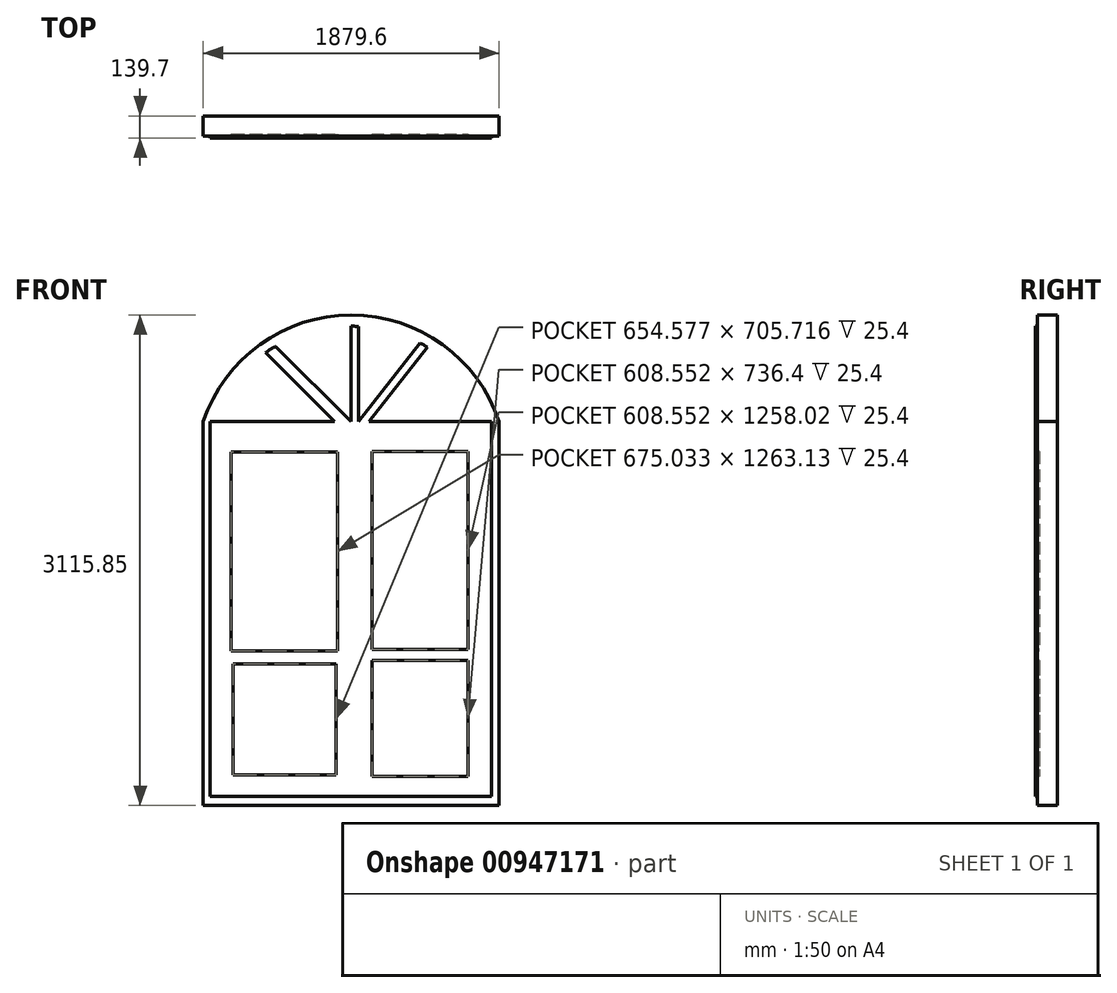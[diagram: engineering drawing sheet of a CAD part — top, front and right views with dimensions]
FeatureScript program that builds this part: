
annotation { "Feature Type Name" : "Feature", "Feature Type Description" : "" }
export const myFeature = defineFeature(function(context is Context, id is Id, definition is map)
    precondition{}
    {
        {
            var Q0;
            Q0=qCreatedBy(makeId("Front.planeOp"),FACE);
            var sketch = newSketch(context, id + "F0", { "sketchPlane" : qUnion([Q0])});
            skLineSegment(sketch, "E0.bottom", {"start": v(0, 0) * mm, "end": v(1879.6, 0) * mm});
            skLineSegment(sketch, "E0.top", {"start": v(0, 2438.4) * mm, "end": v(1879.6, 2438.4) * mm});
            skLineSegment(sketch, "E0.left", {"start": v(0, 0) * mm, "end": v(0, 2438.4) * mm});
            skLineSegment(sketch, "E0.right", {"start": v(1879.6, 0) * mm, "end": v(1879.6, 2438.4) * mm});
            skArc(sketch, "E1", {"start": v(1879.6, 2438.4) * mm, "mid": v(939.8, 3115.85) * mm, "end": v(0, 2438.4) * mm});
            skLineSegment(sketch, "E2.bottom", {"start": v(25.4, 2413) * mm, "end": v(1854.2, 2413) * mm});
            skLineSegment(sketch, "E2.top", {"start": v(25.4, 25.4) * mm, "end": v(1854.2, 25.4) * mm});
            skLineSegment(sketch, "E2.left", {"start": v(25.4, 2413) * mm, "end": v(25.4, 25.4) * mm});
            skLineSegment(sketch, "E2.right", {"start": v(1854.2, 2413) * mm, "end": v(1854.2, 25.4) * mm});
            skSolve(sketch);
        }
        {
            var Q0;
            Q0=makeQuery(id+"F0.imprint","IMPRINT",FACE,{"disambiguationData":[TD([[makeQuery(id+"F0.imprint","IMPRINT",EDGE,{"derivedFrom":sQuery(id+"F0.wireOp",EDGE,"E2.bottom")}),-1.0]])]});
            var Q1;
            Q1=makeQuery(id+"F0.imprint","IMPRINT",FACE,{"disambiguationData":[TD([[makeQuery(id+"F0.imprint","IMPRINT",EDGE,{"derivedFrom":sQuery(id+"F0.wireOp",EDGE,"E0.top")}),1.0]])]});
            var Q2;
            Q2=makeQuery(id+"F0.imprint","IMPRINT",FACE,{"disambiguationData":[TD([[makeQuery(id+"F0.imprint","IMPRINT",EDGE,{"derivedFrom":sQuery(id+"F0.wireOp",EDGE,"E0.bottom")}),1.0]])]});
            extrude(context, id + "F1", {"entities" : qUnion([Q0, Q1, Q2]), "depth" : 127 * mm, "offsetDistance" : 25.4 * mm});
        }
        {
            var Q0;
            Q0=makeQuery(id+"F1.opExtrude","CAP_FACE",FACE,{"disambiguationData":[OSD([sQuery(id+"F0.wireOp",EDGE,"E0.bottom"),sQuery(id+"F0.wireOp",EDGE,"E0.left"),sQuery(id+"F0.wireOp",EDGE,"E0.right"),sQuery(id+"F0.wireOp",EDGE,"E1")])],"isStart":false});
            var sketch = newSketch(context, id + "F2", { "sketchPlane" : qUnion([Q0])});
            skLineSegment(sketch, "E3.bottom", {"start": v(0, 2438.4) * mm, "end": v(1879.6, 2438.4) * mm});
            skLineSegment(sketch, "E3.top", {"start": v(0, 0) * mm, "end": v(1879.6, 0) * mm});
            skLineSegment(sketch, "E3.left", {"start": v(0, 2438.4) * mm, "end": v(0, 0) * mm});
            skLineSegment(sketch, "E3.right", {"start": v(1879.6, 2438.4) * mm, "end": v(1879.6, 0) * mm});
            skLineSegment(sketch, "E4.bottom", {"start": v(1768.5, 81.97) * mm, "end": v(1016.76, 81.97) * mm});
            skLineSegment(sketch, "E4.top", {"start": v(1768.5, 2362.76) * mm, "end": v(1016.76, 2362.76) * mm});
            skLineSegment(sketch, "E4.left", {"start": v(1768.5, 81.97) * mm, "end": v(1768.5, 2362.76) * mm});
            skLineSegment(sketch, "E4.right", {"start": v(1016.76, 81.97) * mm, "end": v(1016.76, 2362.76) * mm});
            skLineSegment(sketch, "E5.bottom", {"start": v(934.94, 2362.76) * mm, "end": v(86.04, 2362.76) * mm});
            skLineSegment(sketch, "E5.top", {"start": v(934.94, 97.3) * mm, "end": v(86.04, 97.3) * mm});
            skLineSegment(sketch, "E5.left", {"start": v(934.94, 2362.76) * mm, "end": v(934.94, 97.3) * mm});
            skLineSegment(sketch, "E5.right", {"start": v(86.04, 2362.76) * mm, "end": v(86.04, 97.3) * mm});
            skLineSegment(sketch, "E6.bottom", {"start": v(178.09, 2245.14) * mm, "end": v(853.12, 2245.14) * mm});
            skLineSegment(sketch, "E6.top", {"start": v(178.09, 982) * mm, "end": v(853.12, 982) * mm});
            skLineSegment(sketch, "E6.left", {"start": v(178.09, 2245.14) * mm, "end": v(178.09, 982) * mm});
            skLineSegment(sketch, "E6.right", {"start": v(853.12, 2245.14) * mm, "end": v(853.12, 982) * mm});
            skLineSegment(sketch, "E7.bottom", {"start": v(188.31, 900.19) * mm, "end": v(842.9, 900.19) * mm});
            skLineSegment(sketch, "E7.top", {"start": v(188.31, 194.47) * mm, "end": v(842.9, 194.47) * mm});
            skLineSegment(sketch, "E7.left", {"start": v(188.31, 900.19) * mm, "end": v(188.31, 194.47) * mm});
            skLineSegment(sketch, "E7.right", {"start": v(842.9, 900.19) * mm, "end": v(842.9, 194.47) * mm});
            skLineSegment(sketch, "E8.bottom", {"start": v(1073.02, 2250.25) * mm, "end": v(1681.57, 2250.25) * mm});
            skLineSegment(sketch, "E8.top", {"start": v(1073.02, 992.24) * mm, "end": v(1681.57, 992.24) * mm});
            skLineSegment(sketch, "E8.left", {"start": v(1073.02, 2250.25) * mm, "end": v(1073.02, 992.24) * mm});
            skLineSegment(sketch, "E8.right", {"start": v(1681.57, 2250.25) * mm, "end": v(1681.57, 992.24) * mm});
            skLineSegment(sketch, "E9.bottom", {"start": v(1073.02, 920.64) * mm, "end": v(1681.57, 920.64) * mm});
            skLineSegment(sketch, "E9.top", {"start": v(1073.02, 184.24) * mm, "end": v(1681.57, 184.24) * mm});
            skLineSegment(sketch, "E9.left", {"start": v(1073.02, 920.64) * mm, "end": v(1073.02, 184.24) * mm});
            skLineSegment(sketch, "E9.right", {"start": v(1681.57, 920.64) * mm, "end": v(1681.57, 184.24) * mm});
            skSolve(sketch);
        }
        {
            var Q0;
            Q0=makeQuery(id+"F2.imprint","IMPRINT",FACE,{"disambiguationData":[TD([[makeQuery(id+"F2.imprint","IMPRINT",EDGE,{"derivedFrom":sQuery(id+"F2.wireOp",EDGE,"E6.bottom")}),-1.0]])]});
            var Q1;
            Q1=makeQuery(id+"F2.imprint","IMPRINT",FACE,{"disambiguationData":[TD([[makeQuery(id+"F2.imprint","IMPRINT",EDGE,{"derivedFrom":sQuery(id+"F2.wireOp",EDGE,"E8.bottom")}),-1.0]])]});
            var Q2;
            Q2=makeQuery(id+"F2.imprint","IMPRINT",FACE,{"disambiguationData":[TD([[makeQuery(id+"F2.imprint","IMPRINT",EDGE,{"derivedFrom":sQuery(id+"F2.wireOp",EDGE,"E9.bottom")}),-1.0]])]});
            var Q3;
            Q3=makeQuery(id+"F2.imprint","IMPRINT",FACE,{"disambiguationData":[TD([[makeQuery(id+"F2.imprint","IMPRINT",EDGE,{"derivedFrom":sQuery(id+"F2.wireOp",EDGE,"E7.bottom")}),-1.0]])]});
            extrude(context, id + "F3", {"entities" : qUnion([Q0, Q1, Q2, Q3]), "operationType" : NewBodyOperationType.REMOVE, "oppositeDirection" : true, "depth" : 12.7 * mm, "offsetDistance" : 25.4 * mm});
        }
        {
            var Q0;
            Q0=makeQuery(id+"F1.opExtrude","CAP_FACE",FACE,{"disambiguationData":[OSD([sQuery(id+"F0.wireOp",EDGE,"E0.bottom"),sQuery(id+"F0.wireOp",EDGE,"E0.left"),sQuery(id+"F0.wireOp",EDGE,"E0.right"),sQuery(id+"F0.wireOp",EDGE,"E1")])],"isStart":false});
            var sketch = newSketch(context, id + "F4", { "sketchPlane" : qUnion([Q0])});
            skLineSegment(sketch, "E10.bottom", {"start": v(45.12, 2438.4) * mm, "end": v(1829.87, 2438.4) * mm});
            skLineSegment(sketch, "E10.top", {"start": v(45.12, 57.49) * mm, "end": v(1829.87, 57.49) * mm});
            skLineSegment(sketch, "E10.left", {"start": v(45.12, 2438.4) * mm, "end": v(45.12, 57.49) * mm});
            skLineSegment(sketch, "E10.right", {"start": v(1829.87, 2438.4) * mm, "end": v(1829.87, 57.49) * mm});
            skLineSegment(sketch, "E11.bottom", {"start": v(937.5, 2438.4) * mm, "end": v(986.08, 2438.4) * mm});
            skLineSegment(sketch, "E11.top", {"start": v(937.5, 57.49) * mm, "end": v(986.08, 57.49) * mm});
            skLineSegment(sketch, "E11.left", {"start": v(937.5, 2438.4) * mm, "end": v(937.5, 57.49) * mm});
            skLineSegment(sketch, "E11.right", {"start": v(986.08, 2438.4) * mm, "end": v(986.08, 57.49) * mm});
            skArc(sketch, "E12", {"start": v(1829.87, 2438.4) * mm, "mid": v(937.5, 3044.76) * mm, "end": v(45.12, 2438.4) * mm});
            skLineSegment(sketch, "E13", {"start": v(937.5, 2438.4) * mm, "end": v(937.5, 3044.76) * mm});
            skLineSegment(sketch, "E14", {"start": v(986.08, 2438.4) * mm, "end": v(986.08, 3043.53) * mm});
            skLineSegment(sketch, "E15", {"start": v(986.08, 2438.4) * mm, "end": v(1377.82, 2937.8) * mm});
            skLineSegment(sketch, "E16", {"start": v(1052.56, 2438.4) * mm, "end": v(1424.22, 2912.2) * mm});
            skLineSegment(sketch, "E17", {"start": v(937.5, 2438.4) * mm, "end": v(459.74, 2917.4) * mm});
            skLineSegment(sketch, "E18", {"start": v(832.66, 2438.4) * mm, "end": v(395.27, 2876.93) * mm});
            skSolve(sketch);
        }
        {
            var Q0;
            {var subQ0=sQuery(id+"F4.wireOp",EDGE,"E17");Q0=makeQuery(id+"F4.imprint","IMPRINT",FACE,{"disambiguationData":[TD([[makeQuery(id+"F4.imprint","IMPRINT",EDGE,{"derivedFrom":subQ0}),1.0]])]});}
            var Q1;
            {var subQ0=sQuery(id+"F4.wireOp",EDGE,"E15");Q1=makeQuery(id+"F4.imprint","IMPRINT",FACE,{"disambiguationData":[TD([[makeQuery(id+"F4.imprint","IMPRINT",EDGE,{"derivedFrom":subQ0}),-1.0]])]});}
            var Q2;
            {var subQ2=sQuery(id+"F4.wireOp",EDGE,"E11.left");Q2=makeQuery(id+"F4.imprint","IMPRINT",FACE,{"disambiguationData":[TD([[makeQuery(id+"F4.imprint","IMPRINT",EDGE,{"derivedFrom":subQ2}),1.0]])]});}
            var Q3;
            {var subQ2=sQuery(id+"F4.wireOp",EDGE,"E13");Q3=makeQuery(id+"F4.imprint","IMPRINT",FACE,{"disambiguationData":[TD([[makeQuery(id+"F4.imprint","IMPRINT",EDGE,{"derivedFrom":subQ2}),-1.0]])]});}
            var Q4;
            {var subQ0=sQuery(id+"F4.wireOp",EDGE,"E10.left");Q4=makeQuery(id+"F4.imprint","IMPRINT",FACE,{"disambiguationData":[TD([[makeQuery(id+"F4.imprint","IMPRINT",EDGE,{"derivedFrom":subQ0}),1.0]])]});}
            var Q5;
            {var subQ1=sQuery(id+"F4.wireOp",EDGE,"E10.right");Q5=makeQuery(id+"F4.imprint","IMPRINT",FACE,{"disambiguationData":[TD([[makeQuery(id+"F4.imprint","IMPRINT",EDGE,{"derivedFrom":subQ1}),-1.0]])]});}
            extrude(context, id + "F5", {"entities" : qUnion([Q0, Q1, Q2, Q3, Q4, Q5]), "operationType" : NewBodyOperationType.ADD, "depth" : 12.7 * mm, "offsetDistance" : 25.4 * mm});
        }
    });
